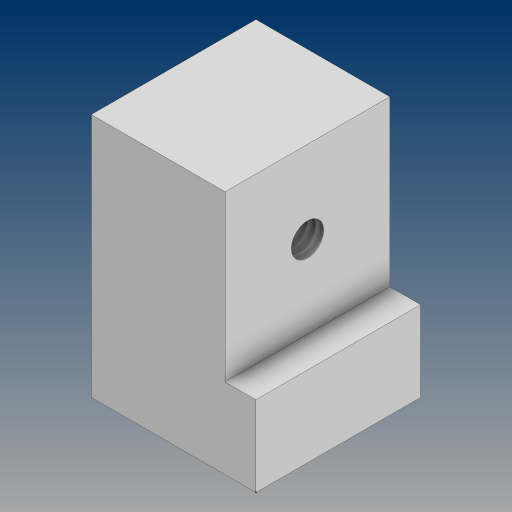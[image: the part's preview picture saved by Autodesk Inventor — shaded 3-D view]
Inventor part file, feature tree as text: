
AUTODESK INVENTOR PART (.ipt)
format: ipt  version: 2024.3 (Build 283343000, 343)  size: 146,944 bytes
history: native  units: in
note: dims shown in document units (in); Inventor stores cm internally (conversion verified against a paired STEP export)
features: sketch x6, extrude x3, hole x3, projected_geometry x1
ambient origin geometry x8: Origin, YZ Plane, XZ Plane, XY Plane, X Axis, Y Axis, Z Axis, Center Point
bodies: Solid1 (feature_tree)
feature tree (13):
  extrude  "Extrusion1"  Depth=1.0in
  hole  "Hole1"  [1 undecoded]
  hole  "Hole2"  [1 undecoded]
  sketch  "Sketch4"  dims[d6=0.196in d7=0.5in d8=0.375in d9=0.25in d10=0.5635in d11=0.75in d12=0.0in d13=0.5in]
  extrude  "Extrusion2"  Depth=0.1875in
  extrude  "Extrusion3"  Depth=1.0in TaperAngle=0.0deg
  hole  "Hole3"  [1 undecoded]
  sketch  "Sketch7"  dims[d15=0.196in d16=0.5in d17=0.375in d18=0.25in d19=0.5635in d20=1.0in d21=0.0in d22=0.1875in d24=1.0in d25=0.0in d26=1.0in d27=0.0in d28=0.5in d29=0.5in d30=0.196in d31=1.0in d32=0.375in d33=0.25in d34=0.5635in d35=1.0in d36=0.0in d23=0.8108in d37=0.75in d38=0.8108in d39=0.0625in d40=0.75in d41=0.375in]
  sketch  "Sketch1"  dims[d0=1.0in d1=1.0in]
  sketch  "Sketch2"  dims[d2=1.488in d3=0.0in d4=0.5in]
  sketch  "Sketch3"  dims[d5=0.5in]
  projected_geometry  "Projected Loop1"
  sketch  "Sketch6"  dims[d14=0.5in]
note: 3 required parameter values undecoded (feature->parameter linkage not recoverable at this tier; creation-order binding heuristic only, values carry confidence <= 0.55)
